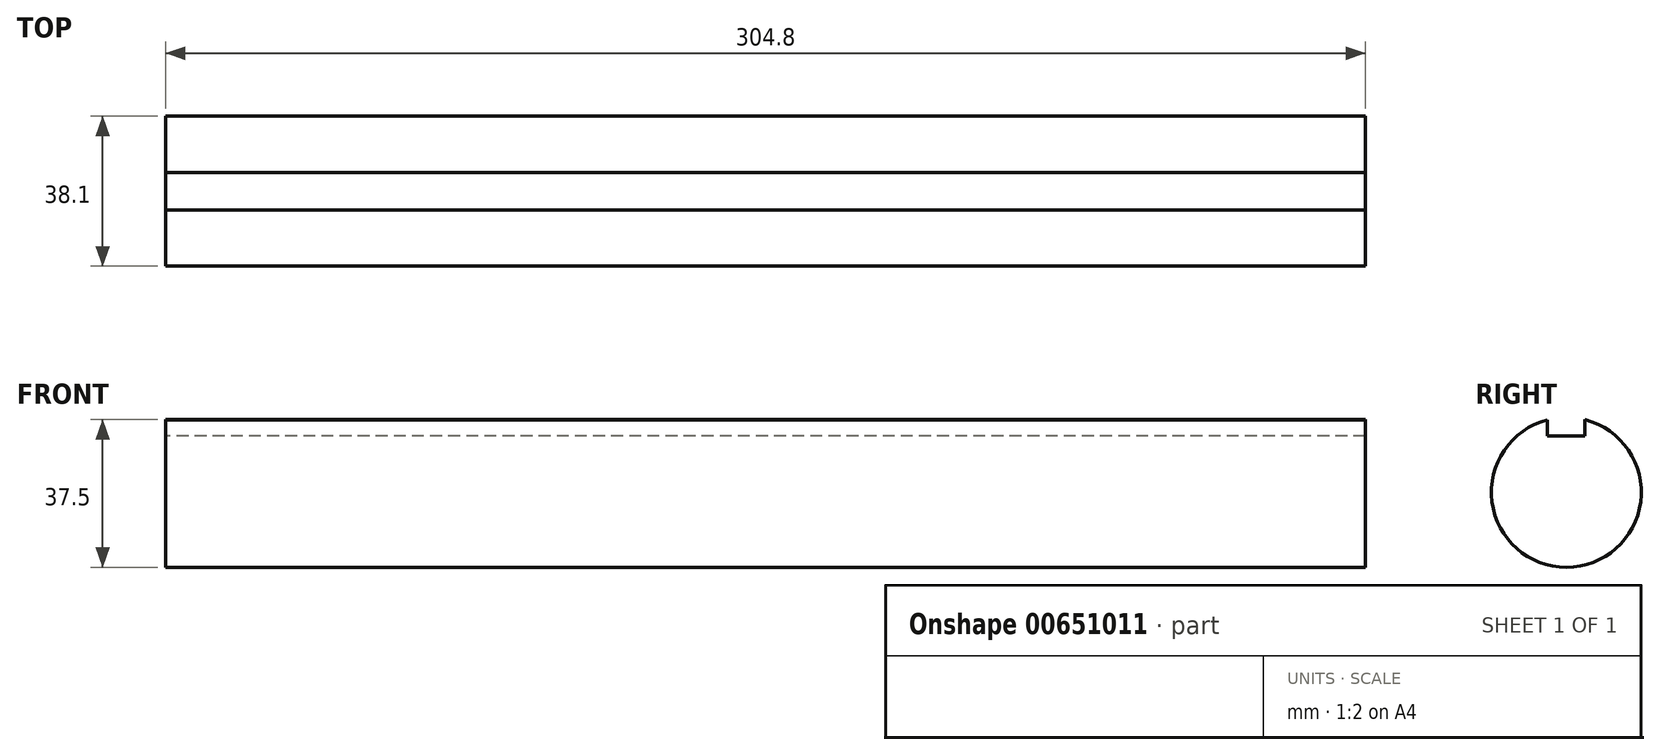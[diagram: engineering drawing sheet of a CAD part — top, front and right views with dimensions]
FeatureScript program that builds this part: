
annotation { "Feature Type Name" : "Feature", "Feature Type Description" : "" }
export const myFeature = defineFeature(function(context is Context, id is Id, definition is map)
    precondition{}
    {
        {
            var Q0;
            Q0=qCreatedBy(makeId("Right.planeOp"),FACE);
            var sketch = newSketch(context, id + "F0", { "sketchPlane" : qUnion([Q0])});
            skLineSegment(sketch, "E0", {"start": v(-4.78, 14.27) * mm, "end": v(4.75, 14.27) * mm});
            skLineSegment(sketch, "E1", {"start": v(4.75, 14.27) * mm, "end": v(4.75, 18.45) * mm});
            skLineSegment(sketch, "E2", {"start": v(-4.78, 14.27) * mm, "end": v(-4.78, 18.44) * mm});
            skArc(sketch, "E3", {"start": v(-4.78, 18.44) * mm, "mid": v(0.01, -19.05) * mm, "end": v(4.75, 18.45) * mm});
            skSolve(sketch);
        }
        {
            var Q0;
            Q0=makeQuery(id+"F0.imprint","IMPRINT",FACE,{"disambiguationData":[TD([[makeQuery(id+"F0.imprint","IMPRINT",EDGE,{"derivedFrom":sQuery(id+"F0.wireOp",EDGE,"E0")}),-1.0]])]});
            extrude(context, id + "F1", {"entities" : qUnion([Q0]), "depth" : 304.8 * mm, "offsetDistance" : 25.4 * mm});
        }
    });
